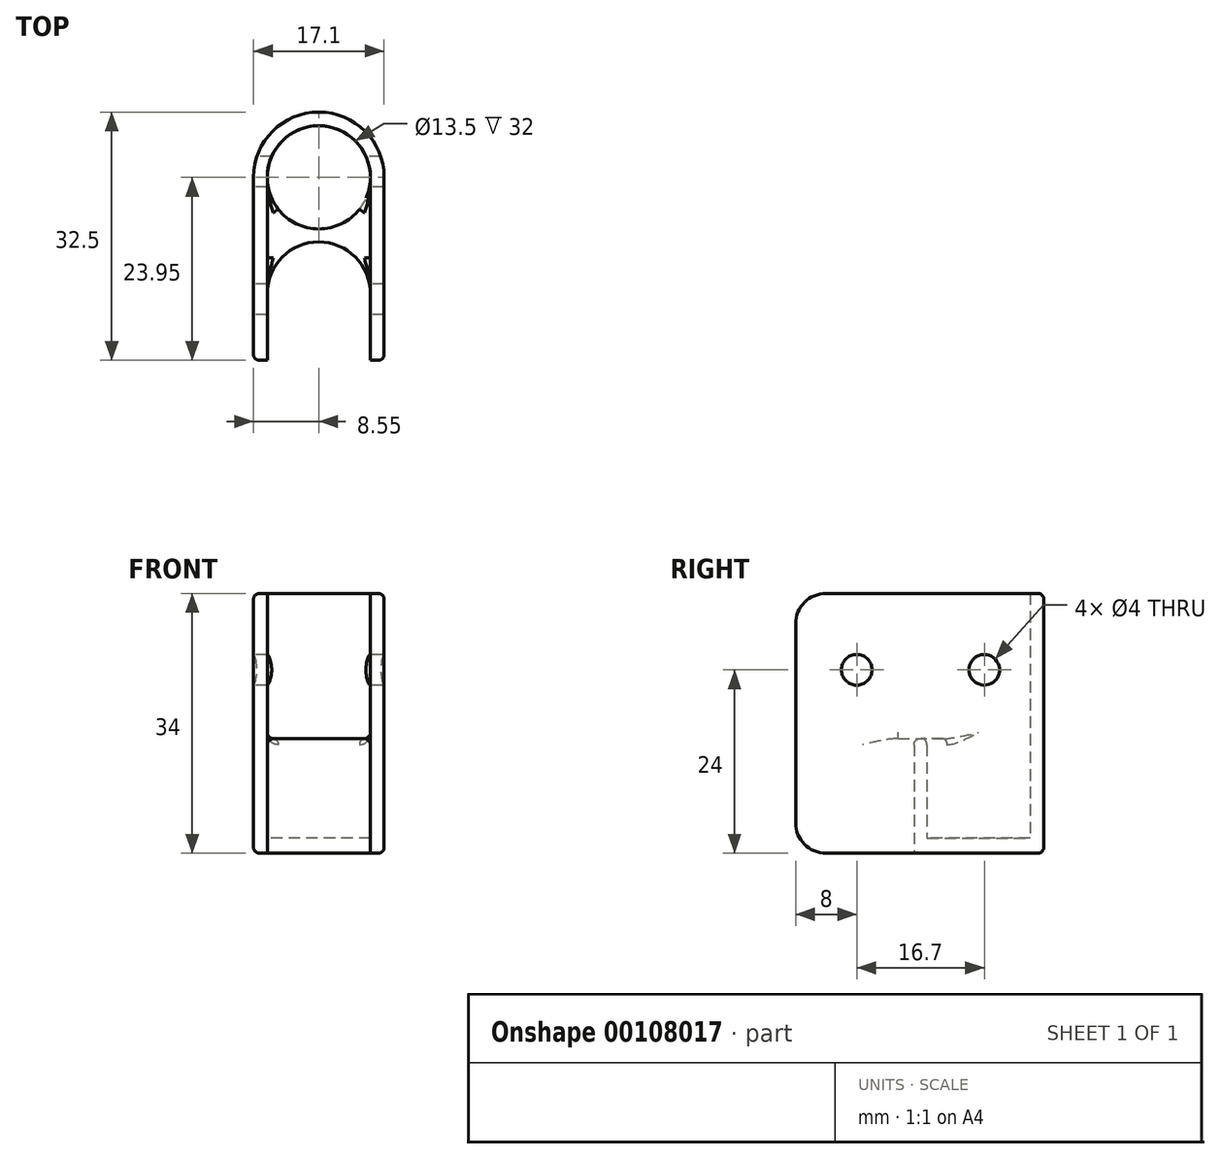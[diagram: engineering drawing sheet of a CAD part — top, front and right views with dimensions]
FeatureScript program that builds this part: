
annotation { "Feature Type Name" : "Feature", "Feature Type Description" : "" }
export const myFeature = defineFeature(function(context is Context, id is Id, definition is map)
    precondition{}
    {
        {
            var Q0;
            Q0=qCreatedBy(makeId("Top.planeOp"),FACE);
            var sketch = newSketch(context, id + "F0", { "sketchPlane" : qUnion([Q0])});
            skCircle(sketch, "E0", {"center": v(0, 7.6) * mm, "radius": 6.75 * mm});
            skArc(sketch, "E1", {"start": v(8.55, 7.6) * mm, "mid": v(0, 16.15) * mm, "end": v(-8.55, 7.6) * mm});
            skLineSegment(sketch, "E2", {"start": v(-8.55, 7.6) * mm, "end": v(-8.55, -16.35) * mm});
            skLineSegment(sketch, "E3", {"start": v(8.55, 7.6) * mm, "end": v(8.55, -16.35) * mm});
            skLineSegment(sketch, "E4", {"start": v(-8.55, -16.35) * mm, "end": v(-6.75, -16.35) * mm});
            skLineSegment(sketch, "E5", {"start": v(-6.75, -16.35) * mm, "end": v(-6.75, -7.6) * mm});
            skLineSegment(sketch, "E6", {"start": v(8.55, -16.35) * mm, "end": v(6.75, -16.35) * mm});
            skLineSegment(sketch, "E7", {"start": v(6.75, -16.35) * mm, "end": v(6.75, -7.6) * mm});
            skArc(sketch, "E8", {"start": v(6.75, -7.6) * mm, "mid": v(0, -0.85) * mm, "end": v(-6.75, -7.6) * mm});
            skPoint(sketch, "E9", {"position": v(0, 16.15) * mm});
            skPoint(sketch, "E10", {"position": v(0, -0.85) * mm});
            skPoint(sketch, "E11", {"position": v(0, 0.85) * mm});
            skSolve(sketch);
        }
        {
            var Q0;
            Q0=makeQuery(id+"F0.imprint","IMPRINT",FACE,{"disambiguationData":[TD([[makeQuery(id+"F0.imprint","IMPRINT",EDGE,{"derivedFrom":sQuery(id+"F0.wireOp",EDGE,"E0")}),-1.0]])]});
            extrude(context, id + "F1", {"entities" : qUnion([Q0]), "depth" : 13 * mm});
        }
        {
            var Q0;
            Q0=makeQuery(id+"F1.opExtrude","CAP_FACE",FACE,{"disambiguationData":[OSD([sQuery(id+"F0.wireOp",EDGE,"E0"),sQuery(id+"F0.wireOp",EDGE,"E1"),sQuery(id+"F0.wireOp",EDGE,"E2"),sQuery(id+"F0.wireOp",EDGE,"E3"),sQuery(id+"F0.wireOp",EDGE,"E4"),sQuery(id+"F0.wireOp",EDGE,"E5"),sQuery(id+"F0.wireOp",EDGE,"E6"),sQuery(id+"F0.wireOp",EDGE,"E7"),sQuery(id+"F0.wireOp",EDGE,"E8")])],"isStart":true});
            var Q1;
            Q1=makeQuery(id+"F0.imprint","IMPRINT",FACE,{"disambiguationData":[TD([[makeQuery(id+"F0.imprint","IMPRINT",EDGE,{"derivedFrom":sQuery(id+"F0.wireOp",EDGE,"E0")}),1.0]])]});
            extrude(context, id + "F2", {"entities" : qUnion([Q0, Q1]), "operationType" : NewBodyOperationType.ADD, "depth" : 2 * mm});
        }
        {
            var Q0;
            Q0=makeQuery(id+"F1.opExtrude","CAP_FACE",FACE,{"disambiguationData":[OSD([sQuery(id+"F0.wireOp",EDGE,"E0"),sQuery(id+"F0.wireOp",EDGE,"E1"),sQuery(id+"F0.wireOp",EDGE,"E2"),sQuery(id+"F0.wireOp",EDGE,"E3"),sQuery(id+"F0.wireOp",EDGE,"E4"),sQuery(id+"F0.wireOp",EDGE,"E5"),sQuery(id+"F0.wireOp",EDGE,"E6"),sQuery(id+"F0.wireOp",EDGE,"E7"),sQuery(id+"F0.wireOp",EDGE,"E8")])],"isStart":false});
            var sketch = newSketch(context, id + "F3", { "sketchPlane" : qUnion([Q0])});
            skArc(sketch, "E12.0", {"start": v(8.55, 7.6) * mm, "mid": v(0, 16.15) * mm, "end": v(-8.55, 7.6) * mm});
            skLineSegment(sketch, "E13.0", {"start": v(-8.55, 7.6) * mm, "end": v(-8.55, -16.35) * mm});
            skLineSegment(sketch, "E14.0", {"start": v(-8.55, -16.35) * mm, "end": v(-6.75, -16.35) * mm});
            skLineSegment(sketch, "E15.0", {"start": v(-6.75, -16.35) * mm, "end": v(-6.75, -7.6) * mm});
            skLineSegment(sketch, "E16.0", {"start": v(6.75, -16.35) * mm, "end": v(6.75, -7.6) * mm});
            skLineSegment(sketch, "E17.0", {"start": v(8.55, -16.35) * mm, "end": v(6.75, -16.35) * mm});
            skLineSegment(sketch, "E18.0", {"start": v(8.55, 7.6) * mm, "end": v(8.55, -16.35) * mm});
            skArc(sketch, "E19.0", {"start": v(6.75, 7.6) * mm, "mid": v(0, 14.35) * mm, "end": v(-6.75, 7.6) * mm});
            skLineSegment(sketch, "E20", {"start": v(-6.75, -7.6) * mm, "end": v(-6.75, 7.6) * mm});
            skLineSegment(sketch, "E21", {"start": v(6.75, -7.6) * mm, "end": v(6.75, 7.6) * mm});
            skSolve(sketch);
        }
        {
            var Q0;
            Q0=makeQuery(id+"F3.imprint","IMPRINT",FACE,{"disambiguationData":[TD([[makeQuery(id+"F3.imprint","IMPRINT",EDGE,{"derivedFrom":sQuery(id+"F3.wireOp",EDGE,"E12.0")}),1.0]])]});
            extrude(context, id + "F4", {"entities" : qUnion([Q0]), "operationType" : NewBodyOperationType.ADD, "depth" : (32 - 13) * mm});
        }
        {
            var Q0;
            {var subQ0=sQuery(id+"F0.wireOp",EDGE,"E2");Q0=makeQuery(id+"F4.boolean.opBoolean","MERGE",FACE,{"derivedFrom":[makeQuery(id+"F2.boolean.opBoolean","MERGE",FACE,{"derivedFrom":[makeQuery(id+"F1.opExtrude","SWEPT_FACE",FACE,{"disambiguationData":[OSD([subQ0])]}),makeQuery(id+"F2.opExtrude","SWEPT_FACE",FACE,{"disambiguationData":[OSD([subQ0])]})]}),makeQuery(id+"F4.opExtrude","SWEPT_FACE",FACE,{"disambiguationData":[OSD([sQuery(id+"F3.wireOp",EDGE,"E13.0")])]})]});}
            var sketch = newSketch(context, id + "F5", { "sketchPlane" : qUnion([Q0])});
            skCircle(sketch, "E22", {"center": v(8.35, 22) * mm, "radius": 2 * mm});
            skCircle(sketch, "E23", {"center": v(-8.35, 22) * mm, "radius": 2 * mm});
            skSolve(sketch);
        }
        {
            var Q0;
            Q0 = qSketchRegion(id + "F5", true);
            extrude(context, id + "F6", {"entities" : qUnion([Q0]), "operationType" : NewBodyOperationType.REMOVE, "endBound" : BoundingType.THROUGH_ALL, "oppositeDirection" : true, "depth" : 25 * mm});
        }
        {
            var Q0;
            Q0=makeQuery(id+"F4.opExtrude","CAP_EDGE",EDGE,{"disambiguationData":[OSD([sQuery(id+"F3.wireOp",EDGE,"E14.0")])],"isStart":false});
            var Q1;
            Q1=makeQuery(id+"F4.opExtrude","CAP_EDGE",EDGE,{"disambiguationData":[OSD([sQuery(id+"F3.wireOp",EDGE,"E17.0")])],"isStart":false});
            var Q2;
            Q2=makeQuery(id+"F2.opExtrude","CAP_EDGE",EDGE,{"disambiguationData":[OSD([sQuery(id+"F0.wireOp",EDGE,"E6")])],"isStart":false});
            var Q3;
            Q3=makeQuery(id+"F2.opExtrude","CAP_EDGE",EDGE,{"disambiguationData":[OSD([sQuery(id+"F0.wireOp",EDGE,"E4")])],"isStart":false});
            fillet(context, id + "F7", {"entities" : qUnion([Q0, Q1, Q2, Q3]), "radius" : 4 * mm, "tangentPropagation" : true, "allowEdgeOverflow" : false});
        }
        {
            var Q0;
            Q0=makeQuery(id+"F4.opExtrude","CAP_EDGE",EDGE,{"disambiguationData":[OSD([sQuery(id+"F3.wireOp",EDGE,"E12.0")])],"isStart":false});
            var Q1;
            Q1=makeQuery(id+"F2.opExtrude","CAP_EDGE",EDGE,{"disambiguationData":[OSD([sQuery(id+"F0.wireOp",EDGE,"E2")])],"isStart":false});
            var Q2;
            {var subQ0=sQuery(id+"F0.wireOp",EDGE,"E4");var subQ1=sQuery(id+"F0.wireOp",EDGE,"E2");Q2=makeQuery(id+"F4.boolean.opBoolean","MERGE",EDGE,{"derivedFrom":[makeQuery(id+"F2.boolean.opBoolean","MERGE",EDGE,{"derivedFrom":[makeQuery(id+"F1.opExtrude","SWEPT_EDGE",EDGE,{"disambiguationData":[OSD([subQ1,subQ0])]}),makeQuery(id+"F2.opExtrude","SWEPT_EDGE",EDGE,{"disambiguationData":[OSD([subQ1,subQ0])]})]}),makeQuery(id+"F4.opExtrude","SWEPT_EDGE",EDGE,{"disambiguationData":[OSD([sQuery(id+"F3.wireOp",EDGE,"E13.0"),sQuery(id+"F3.wireOp",EDGE,"E14.0")])]})]});}
            var Q3;
            {var subQ0=sQuery(id+"F0.wireOp",EDGE,"E6");var subQ1=sQuery(id+"F0.wireOp",EDGE,"E3");Q3=makeQuery(id+"F4.boolean.opBoolean","MERGE",EDGE,{"derivedFrom":[makeQuery(id+"F2.boolean.opBoolean","MERGE",EDGE,{"derivedFrom":[makeQuery(id+"F1.opExtrude","SWEPT_EDGE",EDGE,{"disambiguationData":[OSD([subQ1,subQ0])]}),makeQuery(id+"F2.opExtrude","SWEPT_EDGE",EDGE,{"disambiguationData":[OSD([subQ1,subQ0])]})]}),makeQuery(id+"F4.opExtrude","SWEPT_EDGE",EDGE,{"disambiguationData":[OSD([sQuery(id+"F3.wireOp",EDGE,"E17.0"),sQuery(id+"F3.wireOp",EDGE,"E18.0")])]})]});}
            var Q4;
            Q4=makeQuery(id+"F1.opExtrude","CAP_FACE",FACE,{"disambiguationData":[OSD([sQuery(id+"F0.wireOp",EDGE,"E0"),sQuery(id+"F0.wireOp",EDGE,"E1"),sQuery(id+"F0.wireOp",EDGE,"E2"),sQuery(id+"F0.wireOp",EDGE,"E3"),sQuery(id+"F0.wireOp",EDGE,"E4"),sQuery(id+"F0.wireOp",EDGE,"E5"),sQuery(id+"F0.wireOp",EDGE,"E6"),sQuery(id+"F0.wireOp",EDGE,"E7"),sQuery(id+"F0.wireOp",EDGE,"E8")])],"isStart":false});
            fillet(context, id + "F8", {"entities" : qUnion([Q0, Q1, Q2, Q3, Q4]), "radius" : 0.8 * mm, "tangentPropagation" : true, "allowEdgeOverflow" : false});
        }
    });
